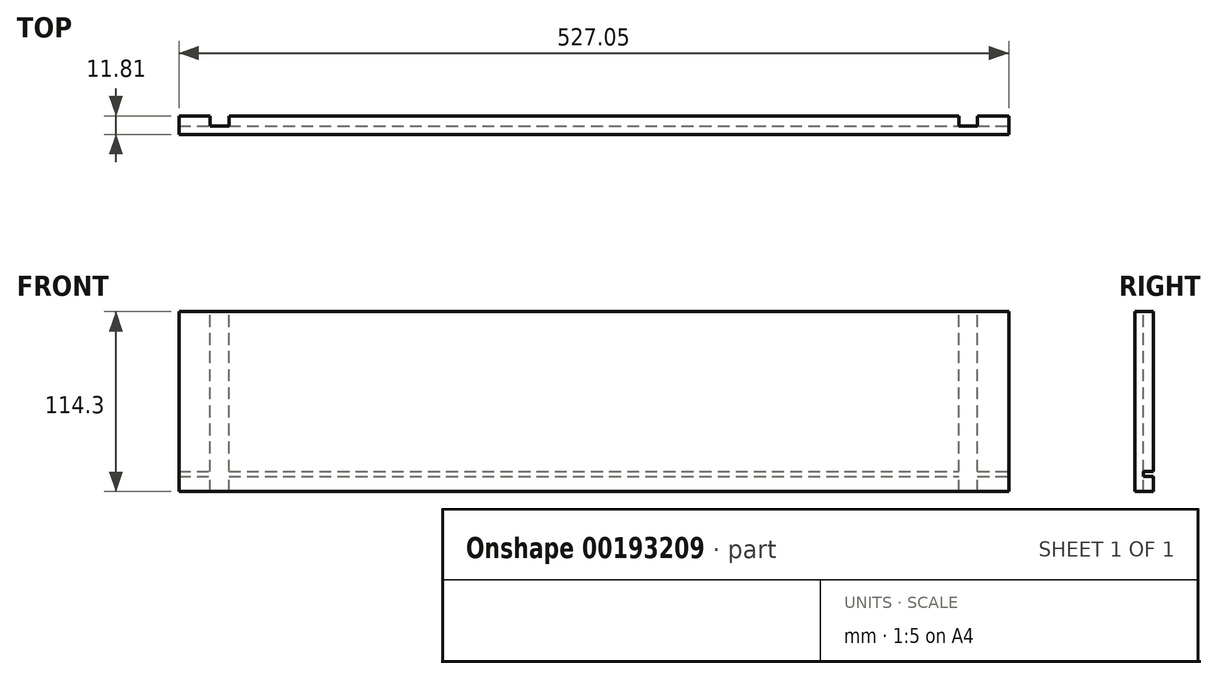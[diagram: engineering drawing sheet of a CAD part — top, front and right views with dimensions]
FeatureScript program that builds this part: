
annotation { "Feature Type Name" : "Feature", "Feature Type Description" : "" }
export const myFeature = defineFeature(function(context is Context, id is Id, definition is map)
    precondition{}
    {
        {
            var Q0;
            Q0=qCreatedBy(makeId("Right.planeOp"),FACE);
            var sketch = newSketch(context, id + "F0", { "sketchPlane" : qUnion([Q0])});
            skLineSegment(sketch, "E0.bottom", {"start": v(-11.81, 0) * mm, "end": v(0, 0) * mm});
            skLineSegment(sketch, "E0.top", {"start": v(-11.81, -114.3) * mm, "end": v(0, -114.3) * mm});
            skLineSegment(sketch, "E0.left", {"start": v(-11.81, 0) * mm, "end": v(-11.81, -101.54) * mm});
            skLineSegment(sketch, "E0.right", {"start": v(0, 0) * mm, "end": v(0, -101.6) * mm});
            skLineSegment(sketch, "E1.trimOffspring", {"start": v(-11.81, -104.72) * mm, "end": v(-11.81, -114.3) * mm});
            skLineSegment(sketch, "E2", {"start": v(-11.81, -101.54) * mm, "end": v(-11.81, -104.72) * mm});
            skLineSegment(sketch, "E3.bottom", {"start": v(0, -101.6) * mm, "end": v(-6.35, -101.6) * mm});
            skLineSegment(sketch, "E3.top", {"start": v(0, -104.78) * mm, "end": v(-6.35, -104.78) * mm});
            skLineSegment(sketch, "E3.right", {"start": v(-6.35, -101.6) * mm, "end": v(-6.35, -104.78) * mm});
            skLineSegment(sketch, "E4.trimOffspring", {"start": v(0, -104.78) * mm, "end": v(0, -114.3) * mm});
            skSolve(sketch);
        }
        {
            var Q0;
            Q0 = qSketchRegion(id + "F0", true);
            extrude(context, id + "F1", {"entities" : qUnion([Q0]), "oppositeDirection" : true, "depth" : 527.05 * mm});
        }
        {
            var Q0;
            Q0=qCreatedBy(makeId("Top.planeOp"),FACE);
            var sketch = newSketch(context, id + "F2", { "sketchPlane" : qUnion([Q0])});
            skLineSegment(sketch, "E5.bottom", {"start": v(-31.75, 0) * mm, "end": v(-19.91, 0) * mm});
            skLineSegment(sketch, "E5.top", {"start": v(-31.75, -6.35) * mm, "end": v(-19.91, -6.35) * mm});
            skLineSegment(sketch, "E5.left", {"start": v(-31.75, 0) * mm, "end": v(-31.75, -6.35) * mm});
            skLineSegment(sketch, "E5.right", {"start": v(-19.91, 0) * mm, "end": v(-19.91, -6.35) * mm});
            skLineSegment(sketch, "E6.bottom", {"start": v(-495.3, 0) * mm, "end": v(-507.14, 0) * mm});
            skLineSegment(sketch, "E6.top", {"start": v(-495.3, -6.35) * mm, "end": v(-507.14, -6.35) * mm});
            skLineSegment(sketch, "E6.left", {"start": v(-495.3, 0) * mm, "end": v(-495.3, -6.35) * mm});
            skLineSegment(sketch, "E6.right", {"start": v(-507.14, 0) * mm, "end": v(-507.14, -6.35) * mm});
            skSolve(sketch);
        }
        {
            var Q0;
            Q0 = qSketchRegion(id + "F2", true);
            extrude(context, id + "F3", {"entities" : qUnion([Q0]), "operationType" : NewBodyOperationType.REMOVE, "endBound" : BoundingType.THROUGH_ALL, "oppositeDirection" : true, "depth" : 25.4 * mm});
        }
    });
